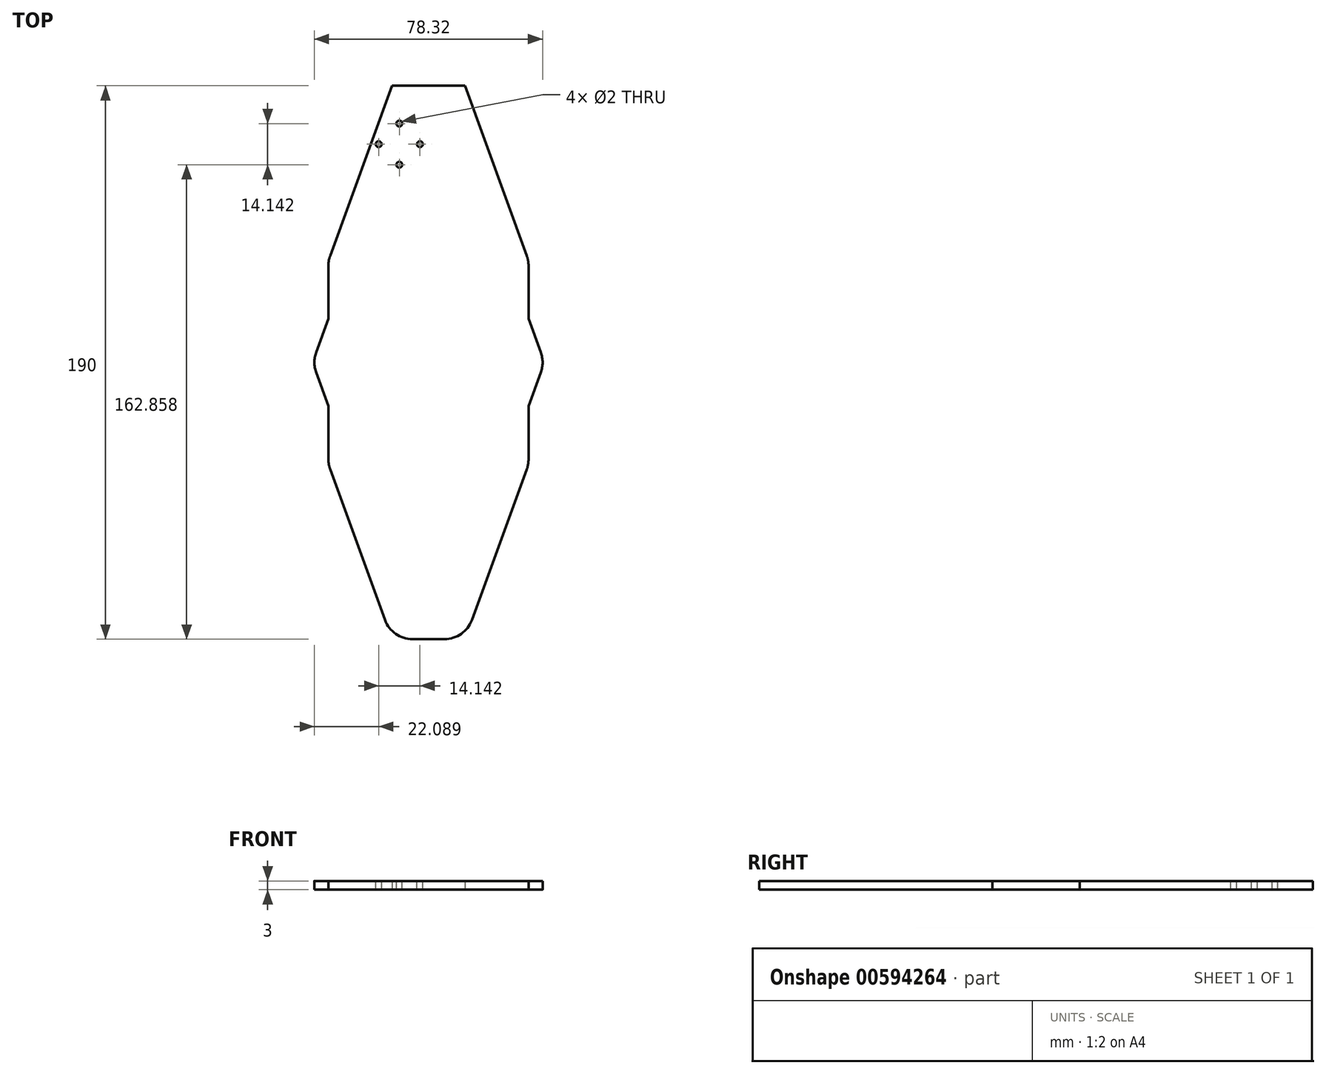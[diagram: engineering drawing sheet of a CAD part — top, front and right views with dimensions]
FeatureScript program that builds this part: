
annotation { "Feature Type Name" : "Feature", "Feature Type Description" : "" }
export const myFeature = defineFeature(function(context is Context, id is Id, definition is map)
    precondition{}
    {
        {
            var Q0;
            Q0=qCreatedBy(makeId("Top.planeOp"),FACE);
            var sketch = newSketch(context, id + "F0", { "sketchPlane" : qUnion([Q0])});
            skCircle(sketch, "E0", {"center": v(0, 0) * mm, "radius": 150 * mm, "construction": true});
            skLineSegment(sketch, "E1", {"start": v(0, 150) * mm, "end": v(0, -150) * mm, "construction": true});
            skLineSegment(sketch, "E2", {"start": v(-34.34, 15) * mm, "end": v(-39.8, 0) * mm});
            skLineSegment(sketch, "E3", {"start": v(-150, 0) * mm, "end": v(150, 0) * mm, "construction": true});
            skLineSegment(sketch, "E4", {"start": v(-34.34, 15) * mm, "end": v(-34.34, 35) * mm});
            skLineSegment(sketch, "E5", {"start": v(-34.34, 35) * mm, "end": v(-12.5, 95) * mm});
            skLineSegment(sketch, "E6", {"start": v(-12.5, 95) * mm, "end": v(0, 95) * mm});
            skLineSegment(sketch, "E7.MirrorCS", {"start": v(12.5, 95) * mm, "end": v(0, 95) * mm});
            skLineSegment(sketch, "E8.MirrorCS", {"start": v(34.34, 35) * mm, "end": v(12.5, 95) * mm});
            skLineSegment(sketch, "E9.MirrorCS", {"start": v(34.34, 15) * mm, "end": v(34.34, 35) * mm});
            skLineSegment(sketch, "E10.MirrorCS", {"start": v(34.34, 15) * mm, "end": v(39.8, 0) * mm});
            skLineSegment(sketch, "E11.MirrorCS", {"start": v(-34.34, -15) * mm, "end": v(-39.8, 0) * mm});
            skLineSegment(sketch, "E12.MirrorCS", {"start": v(-34.34, -15) * mm, "end": v(-34.34, -35) * mm});
            skLineSegment(sketch, "E13.MirrorCS", {"start": v(-34.34, -35) * mm, "end": v(-12.5, -95) * mm});
            skLineSegment(sketch, "E14.MirrorCS", {"start": v(-12.5, -95) * mm, "end": v(0, -95) * mm});
            skLineSegment(sketch, "E15.MirrorCS", {"start": v(12.5, -95) * mm, "end": v(0, -95) * mm});
            skLineSegment(sketch, "E16.MirrorCS", {"start": v(34.34, -35) * mm, "end": v(12.5, -95) * mm});
            skLineSegment(sketch, "E17.MirrorCS", {"start": v(34.34, -15) * mm, "end": v(34.34, -35) * mm});
            skLineSegment(sketch, "E18.MirrorCS", {"start": v(34.34, -15) * mm, "end": v(39.8, 0) * mm});
            skSolve(sketch);
        }
        {
            var Q0;
            Q0 = qSketchRegion(id + "F0", true);
            extrude(context, id + "F1", {"entities" : qUnion([Q0]), "depth" : 3 * mm, "offsetDistance" : 25 * mm, "symmetric" : true});
        }
        {
            var Q0;
            Q0=makeQuery(id+"F1.opExtrude","SWEPT_EDGE",EDGE,{"disambiguationData":[OSD([sQuery(id+"F0.wireOp",EDGE,"E4"),sQuery(id+"F0.wireOp",EDGE,"E5")])]});
            var Q1;
            Q1=makeQuery(id+"F1.opExtrude","SWEPT_EDGE",EDGE,{"disambiguationData":[OSD([sQuery(id+"F0.wireOp",EDGE,"E2"),sQuery(id+"F0.wireOp",EDGE,"E11.MirrorCS")])]});
            var Q2;
            Q2=makeQuery(id+"F1.opExtrude","SWEPT_EDGE",EDGE,{"disambiguationData":[OSD([sQuery(id+"F0.wireOp",EDGE,"E8.MirrorCS"),sQuery(id+"F0.wireOp",EDGE,"E9.MirrorCS")])]});
            var Q3;
            Q3=makeQuery(id+"F1.opExtrude","SWEPT_EDGE",EDGE,{"disambiguationData":[OSD([sQuery(id+"F0.wireOp",EDGE,"E10.MirrorCS"),sQuery(id+"F0.wireOp",EDGE,"E18.MirrorCS")])]});
            var Q4;
            Q4=makeQuery(id+"F1.opExtrude","SWEPT_EDGE",EDGE,{"disambiguationData":[OSD([sQuery(id+"F0.wireOp",EDGE,"E12.MirrorCS"),sQuery(id+"F0.wireOp",EDGE,"E13.MirrorCS")])]});
            var Q5;
            Q5=makeQuery(id+"F1.opExtrude","SWEPT_EDGE",EDGE,{"disambiguationData":[OSD([sQuery(id+"F0.wireOp",EDGE,"E16.MirrorCS"),sQuery(id+"F0.wireOp",EDGE,"E17.MirrorCS")])]});
            var Q6;
            Q6=makeQuery(id+"F1.opExtrude","SWEPT_EDGE",EDGE,{"disambiguationData":[OSD([sQuery(id+"F0.wireOp",EDGE,"E15.MirrorCS"),sQuery(id+"F0.wireOp",EDGE,"E16.MirrorCS")])]});
            var Q7;
            Q7=makeQuery(id+"F1.opExtrude","SWEPT_EDGE",EDGE,{"disambiguationData":[OSD([sQuery(id+"F0.wireOp",EDGE,"E13.MirrorCS"),sQuery(id+"F0.wireOp",EDGE,"E14.MirrorCS")])]});
            fillet(context, id + "F2", {"entities" : qUnion([Q0, Q1, Q2, Q3, Q4, Q5, Q6, Q7]), "radius" : 10 * mm, "tangentPropagation" : true, "allowEdgeOverflow" : false});
        }
        {
            var Q0;
            Q0=makeQuery(id+"F1.opExtrude","CAP_FACE",FACE,{"disambiguationData":[OSD([sQuery(id+"F0.wireOp",EDGE,"E2"),sQuery(id+"F0.wireOp",EDGE,"E4"),sQuery(id+"F0.wireOp",EDGE,"E5"),sQuery(id+"F0.wireOp",EDGE,"E6"),sQuery(id+"F0.wireOp",EDGE,"E7.MirrorCS"),sQuery(id+"F0.wireOp",EDGE,"E8.MirrorCS"),sQuery(id+"F0.wireOp",EDGE,"E9.MirrorCS"),sQuery(id+"F0.wireOp",EDGE,"E10.MirrorCS"),sQuery(id+"F0.wireOp",EDGE,"E11.MirrorCS"),sQuery(id+"F0.wireOp",EDGE,"E12.MirrorCS"),sQuery(id+"F0.wireOp",EDGE,"E13.MirrorCS"),sQuery(id+"F0.wireOp",EDGE,"E14.MirrorCS"),sQuery(id+"F0.wireOp",EDGE,"E15.MirrorCS"),sQuery(id+"F0.wireOp",EDGE,"E16.MirrorCS"),sQuery(id+"F0.wireOp",EDGE,"E17.MirrorCS"),sQuery(id+"F0.wireOp",EDGE,"E18.MirrorCS")])],"isStart":false});
            var sketch = newSketch(context, id + "F3", { "sketchPlane" : qUnion([Q0])});
            skPoint(sketch, "E19", {"position": v(-17.07, 74.93) * mm});
            skPoint(sketch, "E20", {"position": v(-10, 82) * mm});
            skPoint(sketch, "E21", {"position": v(-10, 67.86) * mm});
            skPoint(sketch, "E22", {"position": v(-2.93, 74.93) * mm});
            skLineSegment(sketch, "E23", {"start": v(-10, 74.93) * mm, "end": v(-20.48, 85.41) * mm, "construction": true});
            skLineSegment(sketch, "E24", {"start": v(-17.07, 74.93) * mm, "end": v(-10, 82) * mm, "construction": true});
            skLineSegment(sketch, "E25", {"start": v(-2.93, 74.93) * mm, "end": v(-10, 82) * mm, "construction": true});
            skLineSegment(sketch, "E26", {"start": v(-10, 67.86) * mm, "end": v(-2.93, 74.93) * mm, "construction": true});
            skLineSegment(sketch, "E27", {"start": v(-17.07, 74.93) * mm, "end": v(-10, 67.86) * mm, "construction": true});
            skLineSegment(sketch, "E28", {"start": v(-10, 67.86) * mm, "end": v(-10, 82) * mm, "construction": true});
            skLineSegment(sketch, "E29", {"start": v(-17.07, 74.93) * mm, "end": v(-2.93, 74.93) * mm, "construction": true});
            skPoint(sketch, "E30", {"position": v(-10, 74.93) * mm});
            skLineSegment(sketch, "E31", {"start": v(0, 95) * mm, "end": v(0, -95) * mm, "construction": true});
            skLineSegment(sketch, "E32", {"start": v(-19.16, 0) * mm, "end": v(19.16, 0) * mm, "construction": true});
            skSolve(sketch);
        }
        {
            var Q0;
            Q0=sQuery(id+"F3.wireOp",VERTEX,"E19");
            var Q1;
            Q1=sQuery(id+"F3.wireOp",VERTEX,"E20");
            var Q2;
            Q2=sQuery(id+"F3.wireOp",VERTEX,"E21");
            var Q3;
            Q3=sQuery(id+"F3.wireOp",VERTEX,"E22");
            var Q4;
            Q4=makeQuery(id+"F1.opExtrude","SWEPT_BODY",BODY,{"disambiguationData":[OSD([sQuery(id+"F0.wireOp",EDGE,"E2"),sQuery(id+"F0.wireOp",EDGE,"E4"),sQuery(id+"F0.wireOp",EDGE,"E5"),sQuery(id+"F0.wireOp",EDGE,"E6"),sQuery(id+"F0.wireOp",EDGE,"E7.MirrorCS"),sQuery(id+"F0.wireOp",EDGE,"E8.MirrorCS"),sQuery(id+"F0.wireOp",EDGE,"E9.MirrorCS"),sQuery(id+"F0.wireOp",EDGE,"E10.MirrorCS"),sQuery(id+"F0.wireOp",EDGE,"E11.MirrorCS"),sQuery(id+"F0.wireOp",EDGE,"E12.MirrorCS"),sQuery(id+"F0.wireOp",EDGE,"E13.MirrorCS"),sQuery(id+"F0.wireOp",EDGE,"E14.MirrorCS"),sQuery(id+"F0.wireOp",EDGE,"E15.MirrorCS"),sQuery(id+"F0.wireOp",EDGE,"E16.MirrorCS"),sQuery(id+"F0.wireOp",EDGE,"E17.MirrorCS"),sQuery(id+"F0.wireOp",EDGE,"E18.MirrorCS")])]});
            hole(context, id + "F4", {"style" : HoleStyle.SIMPLE, "endStyle" : HoleEndStyle.THROUGH, "holeDiameter" : 2 * mm, "majorDiameter" : 5 * mm, "isTappedThrough" : true, "tappedDepth" : 12 * mm, "tapClearance" : 3, "locations" : qUnion([Q0, Q1, Q2, Q3]), "scope" : qUnion([Q4])});
        }
    });
